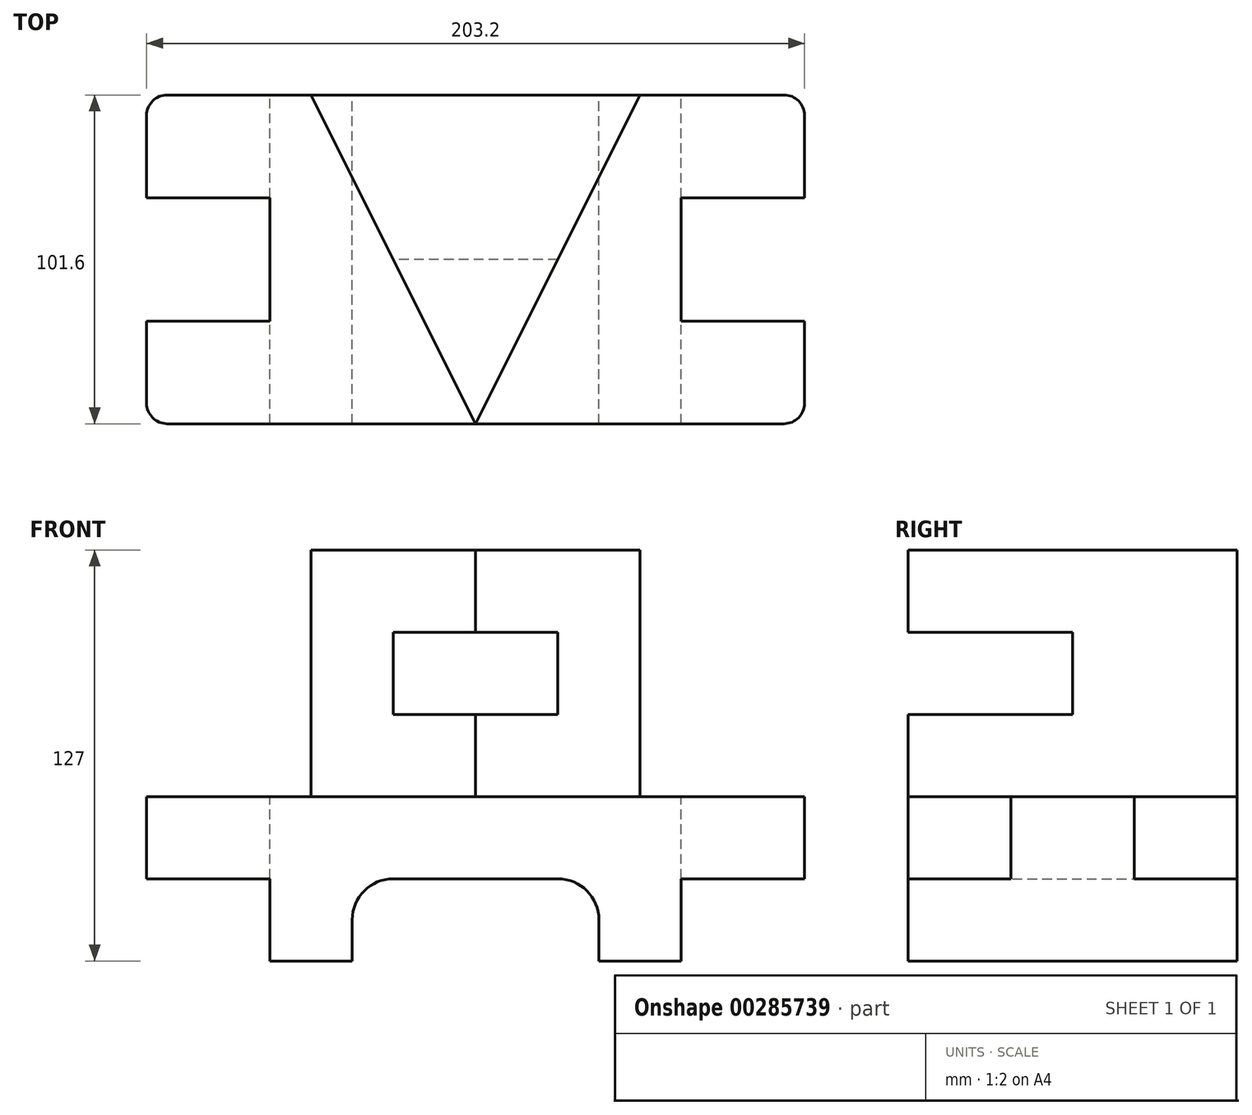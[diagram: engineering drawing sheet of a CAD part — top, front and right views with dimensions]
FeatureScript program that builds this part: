
annotation { "Feature Type Name" : "Feature", "Feature Type Description" : "" }
export const myFeature = defineFeature(function(context is Context, id is Id, definition is map)
    precondition{}
    {
        {
            var Q0;
            Q0=qCreatedBy(makeId("Front.planeOp"),FACE);
            var sketch = newSketch(context, id + "F0", { "sketchPlane" : qUnion([Q0])});
            skLineSegment(sketch, "E0", {"start": v(0, 50.8) * mm, "end": v(127, 50.8) * mm});
            skLineSegment(sketch, "E1", {"start": v(101.6, 0) * mm, "end": v(101.6, 12.7) * mm});
            skLineSegment(sketch, "E2", {"start": v(25.4, 0) * mm, "end": v(25.4, 12.7) * mm});
            skLineSegment(sketch, "E3", {"start": v(38.1, 25.4) * mm, "end": v(88.9, 25.4) * mm});
            skArc(sketch, "E4", {"start": v(25.4, 12.7) * mm, "mid": v(29.12, 21.68) * mm, "end": v(38.1, 25.4) * mm});
            skArc(sketch, "E5", {"start": v(101.6, 12.7) * mm, "mid": v(97.88, 21.68) * mm, "end": v(88.9, 25.4) * mm});
            skLineSegment(sketch, "E6", {"start": v(0, 50.8) * mm, "end": v(0, 0) * mm});
            skLineSegment(sketch, "E7", {"start": v(0, 0) * mm, "end": v(25.4, 0) * mm});
            skLineSegment(sketch, "E8", {"start": v(127, 50.8) * mm, "end": v(127, 0) * mm});
            skLineSegment(sketch, "E9", {"start": v(127, 0) * mm, "end": v(101.6, 0) * mm});
            skSolve(sketch);
        }
        {
            var Q0;
            Q0 = qSketchRegion(id + "F0", true);
            extrude(context, id + "F1", {"entities" : qUnion([Q0]), "depth" : 101.6 * mm});
        }
        {
            var Q0;
            Q0=makeQuery(id+"F1.opExtrude","SWEPT_FACE",FACE,{"disambiguationData":[OSD([sQuery(id+"F0.wireOp",EDGE,"E0")])]});
            var sketch = newSketch(context, id + "F2", { "sketchPlane" : qUnion([Q0])});
            skLineSegment(sketch, "E10", {"start": v(0, 0) * mm, "end": v(0, -101.6) * mm});
            skLineSegment(sketch, "E11", {"start": v(127, -101.6) * mm, "end": v(127, 0) * mm});
            skLineSegment(sketch, "E12", {"start": v(0, -101.6) * mm, "end": v(-31.75, -101.6) * mm});
            skLineSegment(sketch, "E13", {"start": v(0, 0) * mm, "end": v(-31.75, 0) * mm});
            skLineSegment(sketch, "E14", {"start": v(127, 0) * mm, "end": v(158.75, 0) * mm});
            skLineSegment(sketch, "E15", {"start": v(127, -101.6) * mm, "end": v(158.75, -101.6) * mm});
            skArc(sketch, "E16", {"start": v(-38.1, -6.35) * mm, "mid": v(-36.24, -1.86) * mm, "end": v(-31.75, 0) * mm});
            skArc(sketch, "E17", {"start": v(-38.1, -95.25) * mm, "mid": v(-36.24, -99.74) * mm, "end": v(-31.75, -101.6) * mm});
            skArc(sketch, "E18", {"start": v(165.1, -6.35) * mm, "mid": v(163.24, -1.86) * mm, "end": v(158.75, 0) * mm});
            skArc(sketch, "E19", {"start": v(165.1, -95.25) * mm, "mid": v(163.24, -99.74) * mm, "end": v(158.75, -101.6) * mm});
            skLineSegment(sketch, "E20", {"start": v(-38.1, -95.25) * mm, "end": v(-38.1, -6.35) * mm});
            skLineSegment(sketch, "E21", {"start": v(165.1, -6.35) * mm, "end": v(165.1, -95.25) * mm});
            skSolve(sketch);
        }
        {
            var Q0;
            Q0 = qSketchRegion(id + "F2", true);
            extrude(context, id + "F3", {"entities" : qUnion([Q0]), "operationType" : NewBodyOperationType.ADD, "oppositeDirection" : true, "depth" : 25.4 * mm});
        }
        {
            var Q0;
            Q0=makeQuery(id+"F3.boolean.opBoolean","MERGE",FACE,{"derivedFrom":[makeQuery(id+"F1.opExtrude","SWEPT_FACE",FACE,{"disambiguationData":[OSD([sQuery(id+"F0.wireOp",EDGE,"E0")])]}),makeQuery(id+"F3.opExtrude","CAP_FACE",FACE,{"disambiguationData":[OSD([sQuery(id+"F2.wireOp",EDGE,"JjRhpVzg-xW11-wdJc-ffJs-enC58xFFgGAf"),sQuery(id+"F2.wireOp",EDGE,"73f630f3-ee73-4ec3-a1f5-719c41c45fc1"),sQuery(id+"F2.wireOp",EDGE,"94856a3c-541c-4223-835c-25ac4049c8ce"),sQuery(id+"F2.wireOp",EDGE,"E10")])],"isStart":true}),makeQuery(id+"F3.opExtrude","CAP_FACE",FACE,{"disambiguationData":[OSD([sQuery(id+"F2.wireOp",EDGE,"achRhr97-0BX2-oPMQ-I3rZ-AyQKMUz1TOAW"),sQuery(id+"F2.wireOp",EDGE,"8b611b8f-475f-4866-8c46-4a198146147a"),sQuery(id+"F2.wireOp",EDGE,"142c39eb-c878-4924-8ef8-8b2ef5174af1"),sQuery(id+"F2.wireOp",EDGE,"E11")])],"isStart":true})]});
            var sketch = newSketch(context, id + "F4", { "sketchPlane" : qUnion([Q0])});
            skLineSegment(sketch, "E22", {"start": v(12.7, 0) * mm, "end": v(114.3, 0) * mm});
            skLineSegment(sketch, "E23", {"start": v(114.3, 0) * mm, "end": v(63.5, -101.6) * mm});
            skLineSegment(sketch, "E24", {"start": v(63.5, -101.6) * mm, "end": v(12.7, 0) * mm});
            skSolve(sketch);
        }
        {
            var Q0;
            Q0 = qSketchRegion(id + "F4", true);
            extrude(context, id + "F5", {"entities" : qUnion([Q0]), "operationType" : NewBodyOperationType.ADD, "depth" : 76.2 * mm});
        }
        {
            var Q0;
            Q0=qCreatedBy(makeId("Right.planeOp"),FACE);
            var sketch = newSketch(context, id + "F6", { "sketchPlane" : qUnion([Q0])});
            skLineSegment(sketch, "E25", {"start": v(-101.6, 101.6) * mm, "end": v(-101.6, 76.2) * mm});
            skLineSegment(sketch, "E26", {"start": v(-101.6, 76.2) * mm, "end": v(-50.8, 76.2) * mm});
            skLineSegment(sketch, "E27", {"start": v(-50.8, 76.2) * mm, "end": v(-50.8, 101.6) * mm});
            skLineSegment(sketch, "E28", {"start": v(-50.8, 101.6) * mm, "end": v(-101.6, 101.6) * mm});
            skSolve(sketch);
        }
        {
            var Q0;
            Q0 = qSketchRegion(id + "F6", true);
            extrude(context, id + "F7", {"entities" : qUnion([Q0]), "operationType" : NewBodyOperationType.REMOVE, "endBound" : BoundingType.THROUGH_ALL, "depth" : 25.4 * mm});
        }
        {
            var Q0;
            {var subQ0=sQuery(id+"F2.wireOp",EDGE,"E15");var subQ1=sQuery(id+"F2.wireOp",EDGE,"E14");var subQ2=sQuery(id+"F2.wireOp",EDGE,"E13");var subQ3=sQuery(id+"F2.wireOp",EDGE,"E12");var subQ4=sQuery(id+"F2.wireOp",EDGE,"E21");var subQ5=sQuery(id+"F2.wireOp",EDGE,"E19");var subQ6=sQuery(id+"F2.wireOp",EDGE,"E18");var subQ7=makeQuery(id+"F3.opExtrude","CAP_FACE",FACE,{"disambiguationData":[OSD([sQuery(id+"F2.wireOp",EDGE,"E11"),subQ1,subQ0,subQ6,subQ5,subQ4])],"isStart":true});var subQ8=sQuery(id+"F0.wireOp",EDGE,"E0");var subQ9=makeQuery(id+"F1.opExtrude","SWEPT_FACE",FACE,{"disambiguationData":[OSD([subQ8])]});var subQ19=makeQuery(id+"F3.opExtrude","CAP_FACE",FACE,{"disambiguationData":[OSD([sQuery(id+"F2.wireOp",EDGE,"E10"),subQ3,subQ2,sQuery(id+"F2.wireOp",EDGE,"E16"),sQuery(id+"F2.wireOp",EDGE,"E17"),sQuery(id+"F2.wireOp",EDGE,"E20")])],"isStart":true});Q0=makeQuery(id+"F5.boolean.opBoolean","SPLIT",FACE,{"disambiguationData":[TD([makeQuery(id+"F3.opExtrude","SWEPT_FACE",FACE,{"disambiguationData":[OSD([subQ6])]})])],"derivedFrom":makeQuery(id+"F3.boolean.opBoolean","MERGE",FACE,{"derivedFrom":[subQ9,subQ19,subQ7]})});}
            var sketch = newSketch(context, id + "F8", { "sketchPlane" : qUnion([Q0])});
            skLineSegment(sketch, "E29", {"start": v(165.1, -31.75) * mm, "end": v(127, -31.75) * mm});
            skLineSegment(sketch, "E30", {"start": v(127, -31.75) * mm, "end": v(127, -69.85) * mm});
            skLineSegment(sketch, "E31", {"start": v(127, -69.85) * mm, "end": v(165.1, -69.85) * mm});
            skLineSegment(sketch, "E32", {"start": v(165.1, -69.85) * mm, "end": v(165.1, -31.75) * mm});
            skLineSegment(sketch, "E33", {"start": v(-38.1, -31.75) * mm, "end": v(-38.1, -69.85) * mm});
            skLineSegment(sketch, "E34", {"start": v(-38.1, -69.85) * mm, "end": v(0, -69.85) * mm});
            skLineSegment(sketch, "E35", {"start": v(0, -69.85) * mm, "end": v(0, -31.75) * mm});
            skLineSegment(sketch, "E36", {"start": v(0, -31.75) * mm, "end": v(-38.1, -31.75) * mm});
            skSolve(sketch);
        }
        {
            var Q0;
            Q0 = qSketchRegion(id + "F8", true);
            extrude(context, id + "F9", {"entities" : qUnion([Q0]), "operationType" : NewBodyOperationType.REMOVE, "endBound" : BoundingType.THROUGH_ALL, "oppositeDirection" : true, "depth" : 25.4 * mm});
        }
    });
